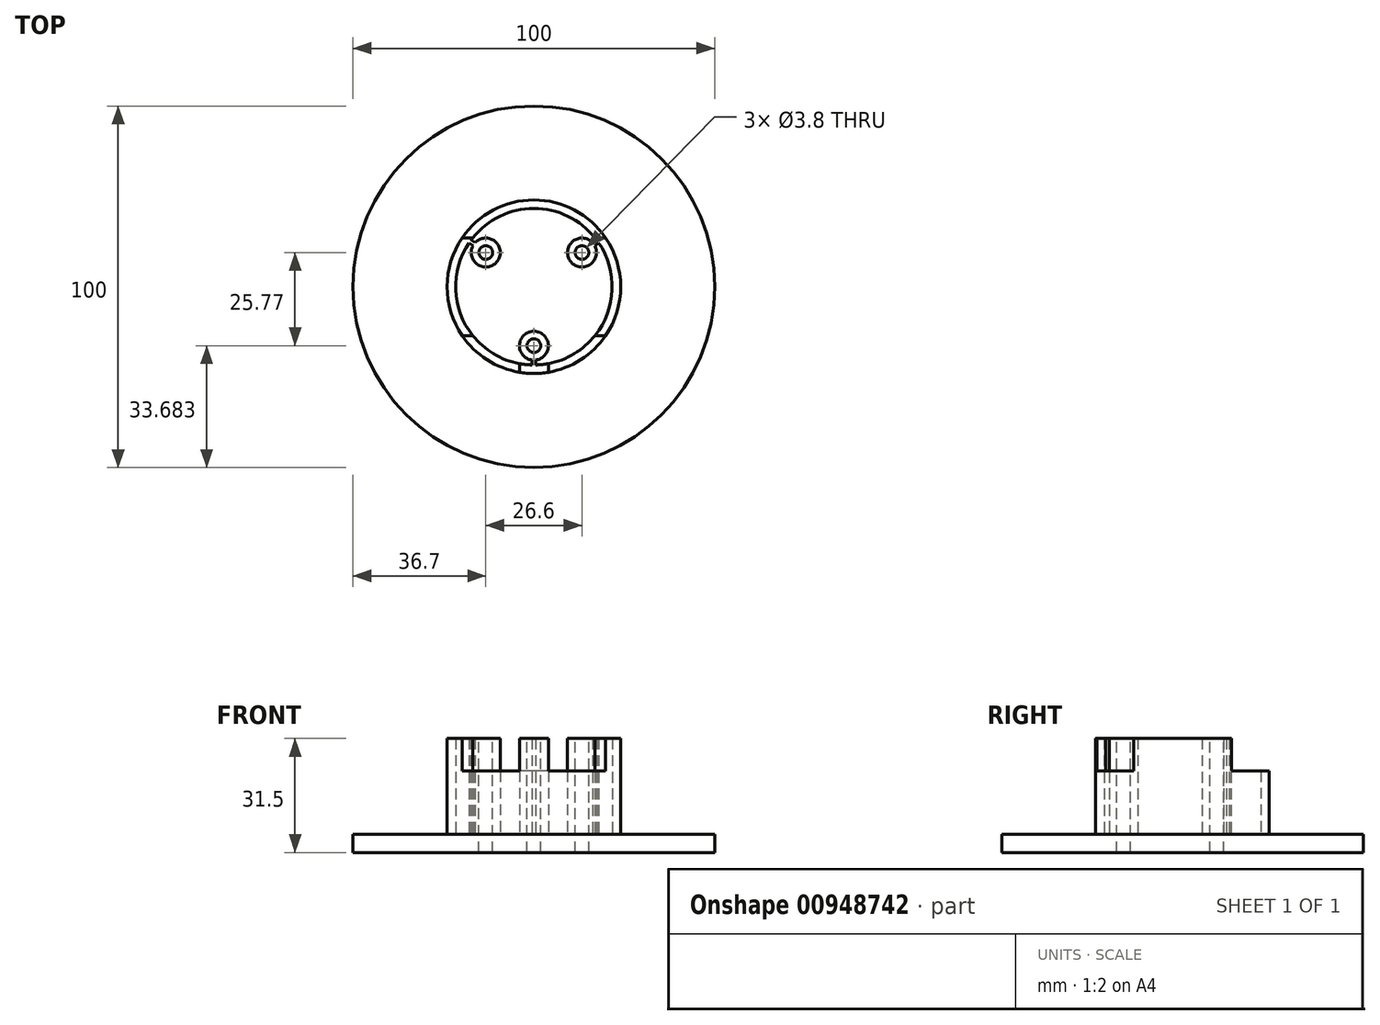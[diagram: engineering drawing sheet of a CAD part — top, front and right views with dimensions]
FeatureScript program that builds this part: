
annotation { "Feature Type Name" : "Feature", "Feature Type Description" : "" }
export const myFeature = defineFeature(function(context is Context, id is Id, definition is map)
    precondition{}
    {
        {
            var Q0;
            Q0=qCreatedBy(makeId("Top.planeOp"),FACE);
            var sketch = newSketch(context, id + "F0", { "sketchPlane" : qUnion([Q0])});
            skCircle(sketch, "E0", {"center": v(0, 0) * mm, "radius": 24 * mm});
            skCircle(sketch, "E1", {"center": v(0, 0) * mm, "radius": 21.65 * mm});
            skLineSegment(sketch, "E2", {"start": v(-19.84, 13.5) * mm, "end": v(19.84, 13.5) * mm, "construction": true});
            skLineSegment(sketch, "E3", {"start": v(-19.84, -13.5) * mm, "end": v(19.84, -13.5) * mm, "construction": true});
            skLineSegment(sketch, "E4", {"start": v(-24, 0) * mm, "end": v(24, 0) * mm, "construction": true});
            skLineSegment(sketch, "E5", {"start": v(0, 24) * mm, "end": v(0, -24) * mm, "construction": true});
            skLineSegment(sketch, "E6", {"start": v(-4, -23.66) * mm, "end": v(-4, -21.28) * mm});
            skLineSegment(sketch, "E7.MirrorCS", {"start": v(4, -23.66) * mm, "end": v(4, -21.28) * mm});
            skCircle(sketch, "E8", {"center": v(0, -16.32) * mm, "radius": 4 * mm});
            skCircle(sketch, "E9", {"center": v(0, -16.32) * mm, "radius": 1.9 * mm});
            skCircle(sketch, "E10.1.0", {"center": v(13.3, 9.45) * mm, "radius": 1.9 * mm});
            skCircle(sketch, "E10.1.1", {"center": v(13.3, 9.45) * mm, "radius": 4 * mm});
            skCircle(sketch, "E10.2.0", {"center": v(-13.3, 9.45) * mm, "radius": 1.9 * mm});
            skCircle(sketch, "E10.2.1", {"center": v(-13.3, 9.45) * mm, "radius": 4 * mm});
            skCircle(sketch, "E11", {"center": v(0, 0) * mm, "radius": 50 * mm});
            skLineSegment(sketch, "E12", {"start": v(-19.84, -13.5) * mm, "end": v(-16.93, -13.5) * mm});
            skLineSegment(sketch, "E13", {"start": v(19.84, -13.5) * mm, "end": v(16.93, -13.5) * mm});
            skLineSegment(sketch, "E14", {"start": v(-19.84, 13.5) * mm, "end": v(-16.93, 13.5) * mm});
            skLineSegment(sketch, "E15", {"start": v(19.84, 13.5) * mm, "end": v(16.93, 13.5) * mm});
            skLineSegment(sketch, "E16", {"start": v(0.5, -21.64) * mm, "end": v(0.5, -20.29) * mm});
            skLineSegment(sketch, "E17.MirrorCS", {"start": v(-0.5, -21.64) * mm, "end": v(-0.5, -20.29) * mm});
            skCircle(sketch, "E18", {"center": v(0, 0) * mm, "radius": 16.32 * mm, "construction": true});
            skLineSegment(sketch, "E19", {"start": v(-13.3, 9.45) * mm, "end": v(13.3, 9.45) * mm, "construction": true});
            skLineSegment(sketch, "E20", {"start": v(0, -16.32) * mm, "end": v(13.3, 9.45) * mm, "construction": true});
            skPoint(sketch, "E21", {"position": v(-11.4, 9.45) * mm});
            skPoint(sketch, "E22", {"position": v(11.4, 9.45) * mm});
            skPoint(sketch, "E23", {"position": v(12.43, 7.76) * mm});
            skPoint(sketch, "E24", {"position": v(0.87, -14.63) * mm});
            skLineSegment(sketch, "E25", {"start": v(0, 0) * mm, "end": v(-17.65, 12.54) * mm, "construction": true});
            skLineSegment(sketch, "E26", {"start": v(-16.25, 12.16) * mm, "end": v(-17.35, 12.95) * mm});
            skLineSegment(sketch, "E27", {"start": v(-16.82, 11.34) * mm, "end": v(-17.93, 12.13) * mm});
            skLineSegment(sketch, "E28.MirrorCS", {"start": v(16.25, 12.16) * mm, "end": v(17.35, 12.95) * mm});
            skLineSegment(sketch, "E29.MirrorCS", {"start": v(16.82, 11.34) * mm, "end": v(17.93, 12.13) * mm});
            skSolve(sketch);
        }
        {
            var Q0;
            Q0=qSketchRegion(id+"F0",true);
            var Q1;
            {var subQ0=sQuery(id+"F0.wireOp",EDGE,"E7.MirrorCS");Q1=makeQuery(id+"F0.imprint","IMPRINT",FACE,{"disambiguationData":[TD([[makeQuery(id+"F0.imprint","IMPRINT",EDGE,{"derivedFrom":subQ0}),-1.0]])]});}
            var Q2;
            {var subQ0=sQuery(id+"F0.wireOp",EDGE,"E13");Q2=makeQuery(id+"F0.imprint","IMPRINT",FACE,{"disambiguationData":[TD([[makeQuery(id+"F0.imprint","IMPRINT",EDGE,{"derivedFrom":subQ0}),-1.0]])]});}
            var Q3;
            {var subQ0=sQuery(id+"F0.wireOp",EDGE,"E16");Q3=makeQuery(id+"F0.imprint","IMPRINT",FACE,{"disambiguationData":[TD([[makeQuery(id+"F0.imprint","IMPRINT",EDGE,{"derivedFrom":subQ0}),-1.0]])]});}
            var Q4;
            {var subQ0=sQuery(id+"F0.wireOp",EDGE,"E14");Q4=makeQuery(id+"F0.imprint","IMPRINT",FACE,{"disambiguationData":[TD([[makeQuery(id+"F0.imprint","IMPRINT",EDGE,{"derivedFrom":subQ0}),1.0]])]});}
            var Q5;
            Q5=makeQuery(id+"F0.imprint","IMPRINT",FACE,{"disambiguationData":[TD([[makeQuery(id+"F0.imprint","IMPRINT",EDGE,{"derivedFrom":sQuery(id+"F0.wireOp",EDGE,"E10.2.0")}),-1.0]])]});
            var Q6;
            Q6=makeQuery(id+"F0.imprint","IMPRINT",FACE,{"disambiguationData":[TD([[makeQuery(id+"F0.imprint","IMPRINT",EDGE,{"derivedFrom":sQuery(id+"F0.wireOp",EDGE,"E10.1.0")}),-1.0]])]});
            var Q7;
            {var subQ0=sQuery(id+"F0.wireOp",EDGE,"ba92d170-98f2-49b8-8035-852a67a62ef7.1.0");Q7=makeQuery(id+"F0.imprint","IMPRINT",FACE,{"disambiguationData":[TD([[makeQuery(id+"F0.imprint","IMPRINT",EDGE,{"derivedFrom":subQ0}),1.0]])]});}
            var Q8;
            {var subQ0=sQuery(id+"F0.wireOp",EDGE,"ba92d170-98f2-49b8-8035-852a67a62ef7.2.0");Q8=makeQuery(id+"F0.imprint","IMPRINT",FACE,{"disambiguationData":[TD([[makeQuery(id+"F0.imprint","IMPRINT",EDGE,{"derivedFrom":subQ0}),1.0]])]});}
            var Q9;
            {var subQ4=sQuery(id+"F0.wireOp",EDGE,"E12");Q9=makeQuery(id+"F0.imprint","IMPRINT",FACE,{"disambiguationData":[TD([[makeQuery(id+"F0.imprint","IMPRINT",EDGE,{"derivedFrom":subQ4}),1.0]])]});}
            var Q10;
            {var subQ0=sQuery(id+"F0.wireOp",EDGE,"E6");Q10=makeQuery(id+"F0.imprint","IMPRINT",FACE,{"disambiguationData":[TD([[makeQuery(id+"F0.imprint","IMPRINT",EDGE,{"derivedFrom":subQ0}),1.0]])]});}
            var Q11;
            {var subQ4=sQuery(id+"F0.wireOp",EDGE,"E6");Q11=makeQuery(id+"F0.imprint","IMPRINT",FACE,{"disambiguationData":[TD([[makeQuery(id+"F0.imprint","IMPRINT",EDGE,{"derivedFrom":subQ4}),-1.0]])]});}
            var Q12;
            Q12=makeQuery(id+"F0.imprint","IMPRINT",FACE,{"disambiguationData":[TD([[makeQuery(id+"F0.imprint","IMPRINT",EDGE,{"derivedFrom":sQuery(id+"F0.wireOp",EDGE,"E9")}),-1.0]])]});
            var Q13;
            {var subQ0=sQuery(id+"F0.wireOp",EDGE,"E16");Q13=makeQuery(id+"F0.imprint","IMPRINT",FACE,{"disambiguationData":[TD([[makeQuery(id+"F0.imprint","IMPRINT",EDGE,{"derivedFrom":subQ0}),1.0]])]});}
            var Q14;
            {var subQ0=sQuery(id+"F0.wireOp",EDGE,"E28.MirrorCS");Q14=makeQuery(id+"F0.imprint","IMPRINT",FACE,{"disambiguationData":[TD([[makeQuery(id+"F0.imprint","IMPRINT",EDGE,{"derivedFrom":subQ0}),-1.0]])]});}
            var Q15;
            {var subQ0=sQuery(id+"F0.wireOp",EDGE,"E26");Q15=makeQuery(id+"F0.imprint","IMPRINT",FACE,{"disambiguationData":[TD([[makeQuery(id+"F0.imprint","IMPRINT",EDGE,{"derivedFrom":subQ0}),1.0]])]});}
            extrude(context, id + "F1", {"entities" : qUnion([Q0, Q1, Q2, Q3, Q4, Q5, Q6, Q7, Q8, Q9, Q10, Q11, Q12, Q13, Q14, Q15]), "oppositeDirection" : true, "depth" : 5 * mm, "offsetDistance" : 25 * mm});
        }
        {
            var Q0;
            {var subQ0=sQuery(id+"F0.wireOp",EDGE,"E7.MirrorCS");Q0=makeQuery(id+"F0.imprint","IMPRINT",FACE,{"disambiguationData":[TD([[makeQuery(id+"F0.imprint","IMPRINT",EDGE,{"derivedFrom":subQ0}),-1.0]])]});}
            var Q1;
            {var subQ0=sQuery(id+"F0.wireOp",EDGE,"E6");Q1=makeQuery(id+"F0.imprint","IMPRINT",FACE,{"disambiguationData":[TD([[makeQuery(id+"F0.imprint","IMPRINT",EDGE,{"derivedFrom":subQ0}),1.0]])]});}
            var Q2;
            {var subQ0=sQuery(id+"F0.wireOp",EDGE,"E14");Q2=makeQuery(id+"F0.imprint","IMPRINT",FACE,{"disambiguationData":[TD([[makeQuery(id+"F0.imprint","IMPRINT",EDGE,{"derivedFrom":subQ0}),1.0]])]});}
            extrude(context, id + "F2", {"entities" : qUnion([Q0, Q1, Q2]), "operationType" : NewBodyOperationType.ADD, "depth" : 17.5 * mm, "offsetDistance" : 25 * mm});
        }
        {
            var Q0;
            {var subQ4=sQuery(id+"F0.wireOp",EDGE,"E12");Q0=makeQuery(id+"F0.imprint","IMPRINT",FACE,{"disambiguationData":[TD([[makeQuery(id+"F0.imprint","IMPRINT",EDGE,{"derivedFrom":subQ4}),1.0]])]});}
            var Q1;
            {var subQ0=sQuery(id+"F0.wireOp",EDGE,"E13");Q1=makeQuery(id+"F0.imprint","IMPRINT",FACE,{"disambiguationData":[TD([[makeQuery(id+"F0.imprint","IMPRINT",EDGE,{"derivedFrom":subQ0}),-1.0]])]});}
            var Q2;
            {var subQ0=sQuery(id+"F0.wireOp",EDGE,"ba92d170-98f2-49b8-8035-852a67a62ef7.1.0");Q2=makeQuery(id+"F0.imprint","IMPRINT",FACE,{"disambiguationData":[TD([[makeQuery(id+"F0.imprint","IMPRINT",EDGE,{"derivedFrom":subQ0}),1.0]])]});}
            var Q3;
            Q3=makeQuery(id+"F0.imprint","IMPRINT",FACE,{"disambiguationData":[TD([[makeQuery(id+"F0.imprint","IMPRINT",EDGE,{"derivedFrom":sQuery(id+"F0.wireOp",EDGE,"E10.1.0")}),-1.0]])]});
            var Q4;
            Q4=makeQuery(id+"F0.imprint","IMPRINT",FACE,{"disambiguationData":[TD([[makeQuery(id+"F0.imprint","IMPRINT",EDGE,{"derivedFrom":sQuery(id+"F0.wireOp",EDGE,"E9")}),-1.0]])]});
            var Q5;
            {var subQ0=sQuery(id+"F0.wireOp",EDGE,"E16");Q5=makeQuery(id+"F0.imprint","IMPRINT",FACE,{"disambiguationData":[TD([[makeQuery(id+"F0.imprint","IMPRINT",EDGE,{"derivedFrom":subQ0}),1.0]])]});}
            var Q6;
            {var subQ4=sQuery(id+"F0.wireOp",EDGE,"E6");Q6=makeQuery(id+"F0.imprint","IMPRINT",FACE,{"disambiguationData":[TD([[makeQuery(id+"F0.imprint","IMPRINT",EDGE,{"derivedFrom":subQ4}),-1.0]])]});}
            var Q7;
            {var subQ0=sQuery(id+"F0.wireOp",EDGE,"ba92d170-98f2-49b8-8035-852a67a62ef7.2.0");Q7=makeQuery(id+"F0.imprint","IMPRINT",FACE,{"disambiguationData":[TD([[makeQuery(id+"F0.imprint","IMPRINT",EDGE,{"derivedFrom":subQ0}),1.0]])]});}
            var Q8;
            Q8=makeQuery(id+"F0.imprint","IMPRINT",FACE,{"disambiguationData":[TD([[makeQuery(id+"F0.imprint","IMPRINT",EDGE,{"derivedFrom":sQuery(id+"F0.wireOp",EDGE,"E10.2.0")}),-1.0]])]});
            var Q9;
            {var subQ0=sQuery(id+"F0.wireOp",EDGE,"E26");Q9=makeQuery(id+"F0.imprint","IMPRINT",FACE,{"disambiguationData":[TD([[makeQuery(id+"F0.imprint","IMPRINT",EDGE,{"derivedFrom":subQ0}),1.0]])]});}
            var Q10;
            {var subQ0=sQuery(id+"F0.wireOp",EDGE,"E28.MirrorCS");Q10=makeQuery(id+"F0.imprint","IMPRINT",FACE,{"disambiguationData":[TD([[makeQuery(id+"F0.imprint","IMPRINT",EDGE,{"derivedFrom":subQ0}),-1.0]])]});}
            extrude(context, id + "F3", {"entities" : qUnion([Q0, Q1, Q2, Q3, Q4, Q5, Q6, Q7, Q8, Q9, Q10]), "operationType" : NewBodyOperationType.ADD, "depth" : (17.5 + 9) * mm, "offsetDistance" : 25 * mm});
        }
    });
